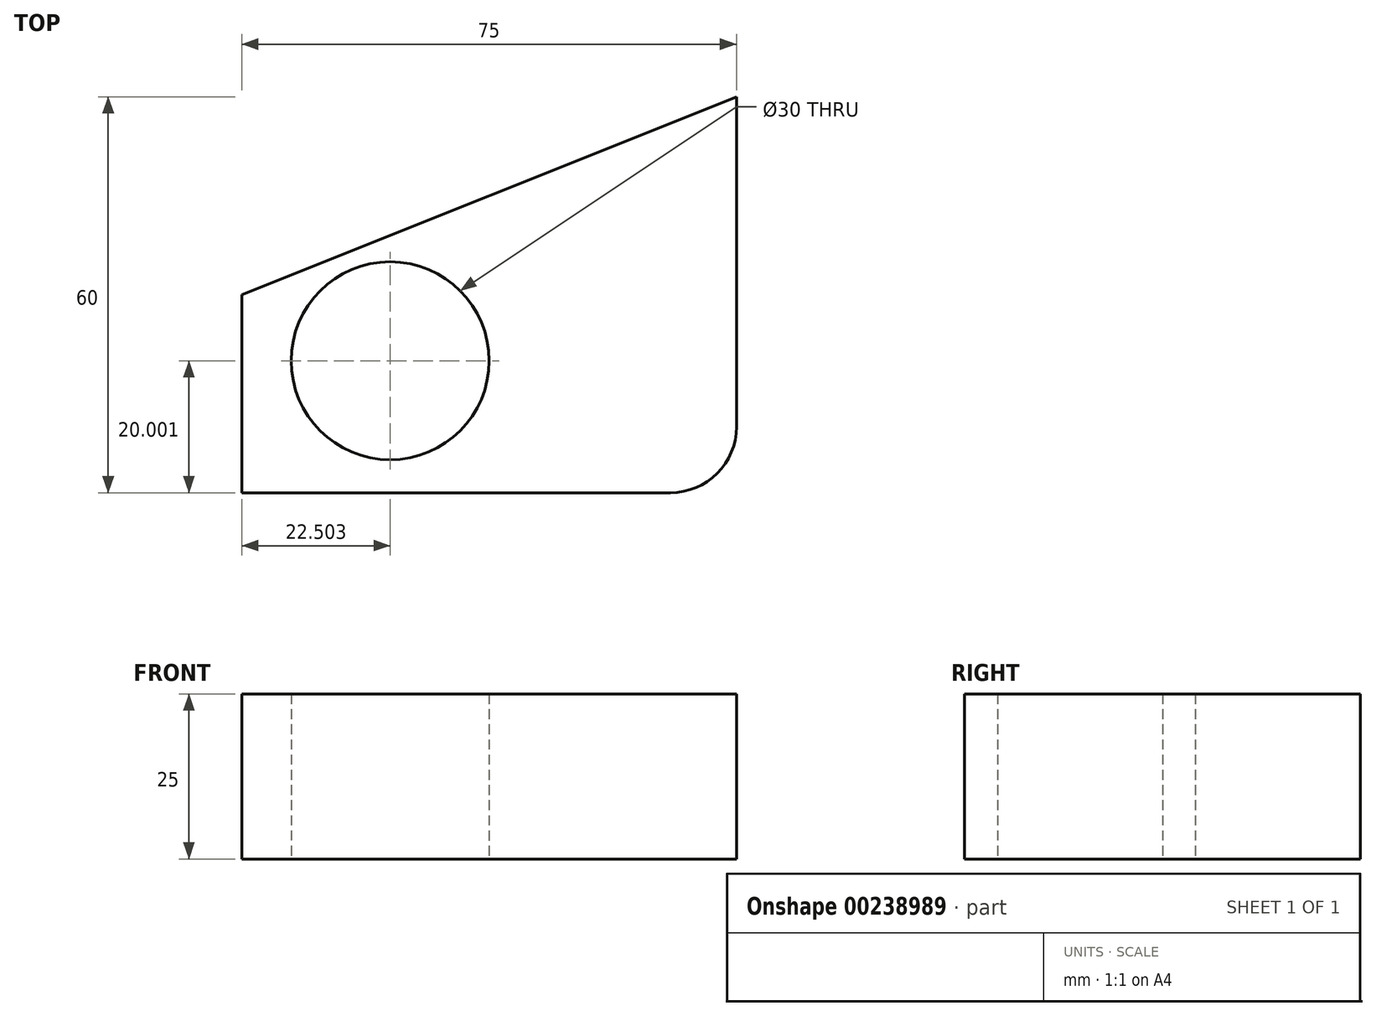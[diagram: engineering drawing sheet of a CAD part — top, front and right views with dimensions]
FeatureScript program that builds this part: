
annotation { "Feature Type Name" : "Feature", "Feature Type Description" : "" }
export const myFeature = defineFeature(function(context is Context, id is Id, definition is map)
    precondition{}
    {
        {
            var Q0;
            Q0=qCreatedBy(makeId("Top.planeOp"),FACE);
            var sketch = newSketch(context, id + "F0", { "sketchPlane" : qUnion([Q0])});
            skLineSegment(sketch, "E0", {"start": v(-49.17, -29.22) * mm, "end": v(15.83, -29.22) * mm});
            skLineSegment(sketch, "E1", {"start": v(25.83, -19.22) * mm, "end": v(25.83, 30.78) * mm});
            skLineSegment(sketch, "E2", {"start": v(-49.17, -29.22) * mm, "end": v(-49.17, 0.78) * mm});
            skLineSegment(sketch, "E3", {"start": v(-49.17, 0.78) * mm, "end": v(25.83, 30.78) * mm});
            skPoint(sketch, "E4.visualSharp", {"position": v(25.83, -29.22) * mm});
            skArc(sketch, "E4.filletArc", {"start": v(15.83, -29.22) * mm, "mid": v(22.9, -26.29) * mm, "end": v(25.83, -19.22) * mm});
            skLineSegment(sketch, "E5", {"start": v(-49.17, -29.22) * mm, "end": v(-26.67, -29.22) * mm});
            skLineSegment(sketch, "E6", {"start": v(-26.67, -29.22) * mm, "end": v(-26.67, -9.22) * mm});
            skCircle(sketch, "E7", {"center": v(-26.67, -9.22) * mm, "radius": 15 * mm});
            skSolve(sketch);
        }
        {
            var Q0;
            Q0 = qSketchRegion(id + "F0", true);
            extrude(context, id + "F1", {"entities" : qUnion([Q0]), "depth" : 25 * mm});
        }
    });
